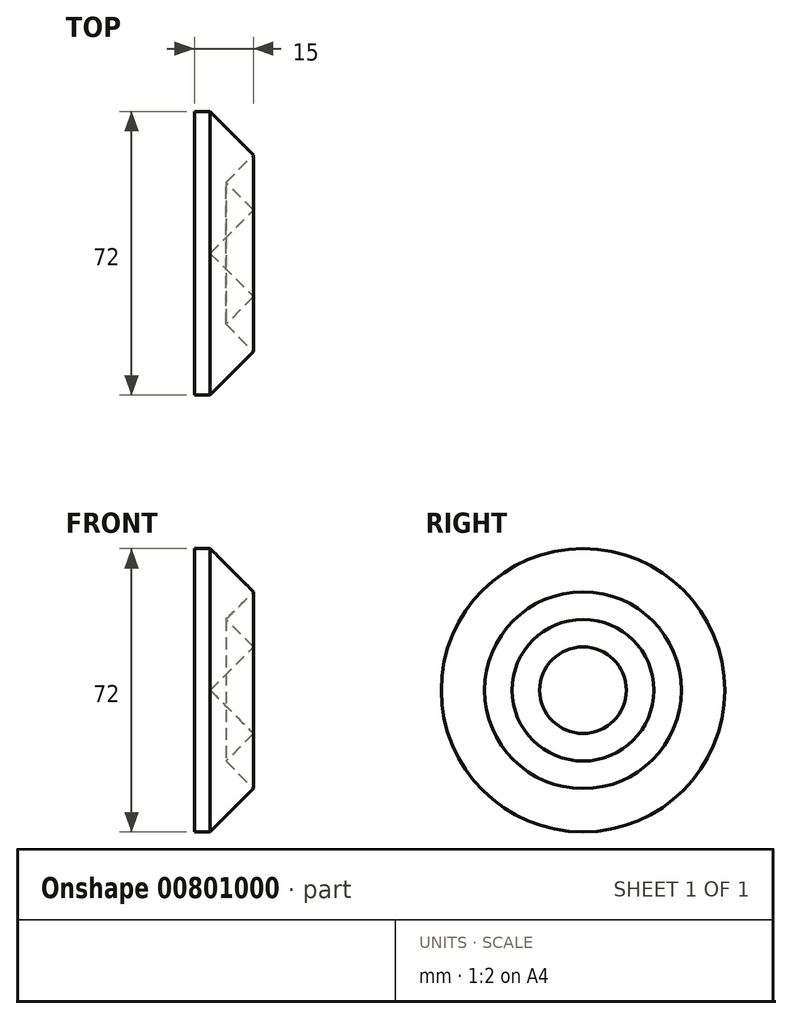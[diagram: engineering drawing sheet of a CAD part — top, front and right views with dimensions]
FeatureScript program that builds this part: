
annotation { "Feature Type Name" : "Feature", "Feature Type Description" : "" }
export const myFeature = defineFeature(function(context is Context, id is Id, definition is map)
    precondition{}
    {
        {
            var Q0;
            Q0=qCreatedBy(makeId("Top.planeOp"),FACE);
            var sketch = newSketch(context, id + "F0", { "sketchPlane" : qUnion([Q0])});
            skLineSegment(sketch, "E0", {"start": v(0, 0) * mm, "end": v(0, -36) * mm});
            skLineSegment(sketch, "E1", {"start": v(0, -36) * mm, "end": v(4, -36) * mm});
            skLineSegment(sketch, "E2", {"start": v(0, 0) * mm, "end": v(4, 0) * mm});
            skLineSegment(sketch, "E3", {"start": v(4, -4) * mm, "end": v(4, -32) * mm});
            skLineSegment(sketch, "E4", {"start": v(4, 0) * mm, "end": v(15, -11) * mm});
            skLineSegment(sketch, "E5", {"start": v(15, -25) * mm, "end": v(4, -36) * mm});
            skLineSegment(sketch, "E6", {"start": v(4, -4) * mm, "end": v(11, -11) * mm});
            skLineSegment(sketch, "E7", {"start": v(15, -11) * mm, "end": v(8.02, -18) * mm});
            skLineSegment(sketch, "E8", {"start": v(8.02, -18) * mm, "end": v(15, -25) * mm});
            skLineSegment(sketch, "E9", {"start": v(4, -32) * mm, "end": v(11, -25) * mm});
            skLineSegment(sketch, "E10", {"start": v(11, -11) * mm, "end": v(15, -11) * mm, "construction": true});
            skLineSegment(sketch, "E11", {"start": v(11, -25) * mm, "end": v(4, -18.1) * mm});
            skLineSegment(sketch, "E12", {"start": v(4, -18.1) * mm, "end": v(4, -17.9) * mm});
            skLineSegment(sketch, "E13", {"start": v(4, -17.9) * mm, "end": v(11, -11) * mm});
            skLineSegment(sketch, "E14", {"start": v(8.02, -18) * mm, "end": v(4, -18) * mm, "construction": true});
            skSolve(sketch);
        }
        {
            var Q0;
            {var subQ0=sQuery(id+"F0.wireOp",EDGE,"E6");Q0=makeQuery(id+"F0.imprint","IMPRINT",FACE,{"disambiguationData":[TD([[makeQuery(id+"F0.imprint","IMPRINT",EDGE,{"derivedFrom":subQ0}),-1.0]])]});}
            var Q1;
            Q1=makeQuery(id+"F0.imprint","IMPRINT",FACE,{"disambiguationData":[TD([[makeQuery(id+"F0.imprint","IMPRINT",EDGE,{"derivedFrom":sQuery(id+"F0.wireOp",EDGE,"E0")}),1.0]])]});
            var Q2;
            {var subQ0=sQuery(id+"F0.wireOp",EDGE,"E9");Q2=makeQuery(id+"F0.imprint","IMPRINT",FACE,{"disambiguationData":[TD([[makeQuery(id+"F0.imprint","IMPRINT",EDGE,{"derivedFrom":subQ0}),1.0]])]});}
            var Q3;
            Q3=sQuery(id+"F0.wireOp",EDGE,"E2");
            revolve(context, id + "F1", {"surfaceOperationType" : NewSurfaceOperationType.NEW, "entities" : qUnion([Q0, Q1, Q2]), "axis" : qUnion([Q3]), "revolveType" : RevolveType.FULL});
        }
    });
